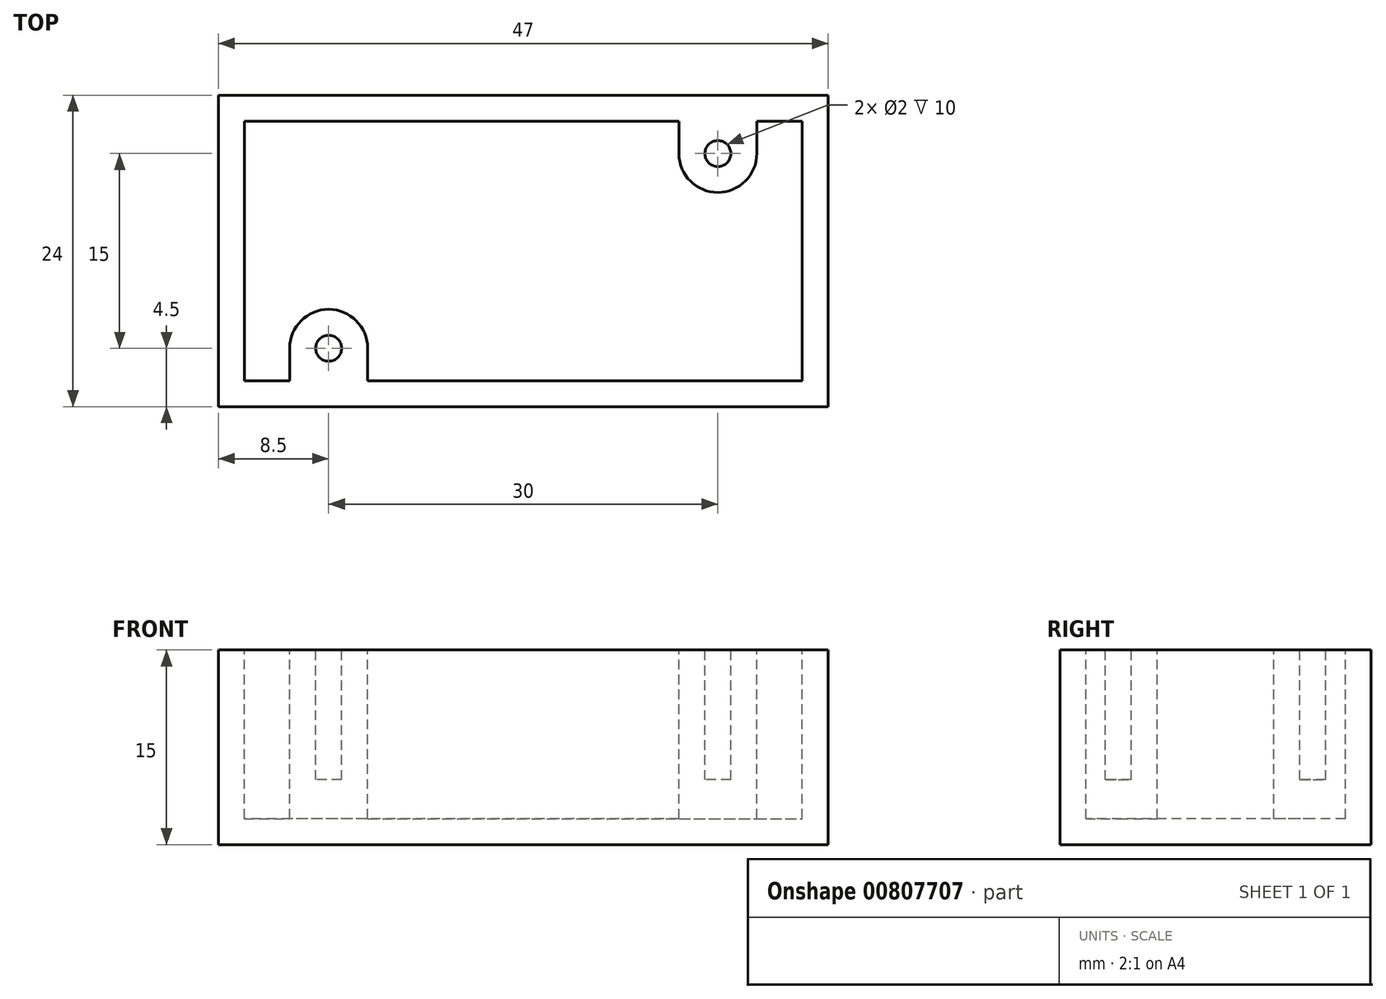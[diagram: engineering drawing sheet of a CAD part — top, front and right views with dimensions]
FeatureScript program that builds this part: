
annotation { "Feature Type Name" : "Feature", "Feature Type Description" : "" }
export const myFeature = defineFeature(function(context is Context, id is Id, definition is map)
    precondition{}
    {
        {
            var Q0;
            Q0=qCreatedBy(makeId("Top.planeOp"),FACE);
            var sketch = newSketch(context, id + "F0", { "sketchPlane" : qUnion([Q0])});
            skLineSegment(sketch, "E0.bottom", {"start": v(-23.5, 12) * mm, "end": v(23.5, 12) * mm});
            skLineSegment(sketch, "E0.top", {"start": v(-23.5, -12) * mm, "end": v(23.5, -12) * mm});
            skLineSegment(sketch, "E0.left", {"start": v(-23.5, 12) * mm, "end": v(-23.5, -12) * mm});
            skLineSegment(sketch, "E0.right", {"start": v(23.5, 12) * mm, "end": v(23.5, -12) * mm});
            skSolve(sketch);
        }
        {
            var Q0;
            Q0 = qSketchRegion(id + "F0", true);
            extrude(context, id + "F1", {"entities" : qUnion([Q0]), "depth" : 15 * mm, "offsetDistance" : 25 * mm});
        }
        {
            var Q0;
            Q0=makeQuery(id+"F1.opExtrude","CAP_FACE",FACE,{"disambiguationData":[OSD([sQuery(id+"F0.wireOp",EDGE,"E0.bottom"),sQuery(id+"F0.wireOp",EDGE,"E0.top"),sQuery(id+"F0.wireOp",EDGE,"E0.left"),sQuery(id+"F0.wireOp",EDGE,"E0.right")])],"isStart":false});
            var sketch = newSketch(context, id + "F2", { "sketchPlane" : qUnion([Q0])});
            skLineSegment(sketch, "E1", {"start": v(18, 10) * mm, "end": v(21.5, 10) * mm});
            skLineSegment(sketch, "E2", {"start": v(21.5, 10) * mm, "end": v(21.5, -10) * mm});
            skLineSegment(sketch, "E3", {"start": v(18, 10) * mm, "end": v(18, 7.5) * mm});
            skArc(sketch, "E4", {"start": v(12, 7.5) * mm, "mid": v(15, 4.5) * mm, "end": v(18, 7.5) * mm});
            skLineSegment(sketch, "E5", {"start": v(12, 7.5) * mm, "end": v(12, 10) * mm});
            skLineSegment(sketch, "E6", {"start": v(12, 10) * mm, "end": v(-21.5, 10) * mm});
            skLineSegment(sketch, "E7", {"start": v(-21.5, 10) * mm, "end": v(-21.5, -10) * mm});
            skLineSegment(sketch, "E8", {"start": v(-21.5, -10) * mm, "end": v(-18, -10) * mm});
            skLineSegment(sketch, "E9", {"start": v(-18, -10) * mm, "end": v(-18, -7.5) * mm});
            skArc(sketch, "E10", {"start": v(-12, -7.5) * mm, "mid": v(-15, -4.5) * mm, "end": v(-18, -7.5) * mm});
            skLineSegment(sketch, "E11", {"start": v(-12, -7.5) * mm, "end": v(-12, -10) * mm});
            skLineSegment(sketch, "E12", {"start": v(-12, -10) * mm, "end": v(21.5, -10) * mm});
            skSolve(sketch);
        }
        {
            var Q0;
            Q0 = qSketchRegion(id + "F2", true);
            extrude(context, id + "F3", {"entities" : qUnion([Q0]), "operationType" : NewBodyOperationType.REMOVE, "oppositeDirection" : true, "depth" : 13 * mm, "offsetDistance" : 25 * mm});
        }
        {
            var Q0;
            Q0=makeQuery(id+"F1.opExtrude","CAP_FACE",FACE,{"disambiguationData":[OSD([sQuery(id+"F0.wireOp",EDGE,"E0.bottom"),sQuery(id+"F0.wireOp",EDGE,"E0.top"),sQuery(id+"F0.wireOp",EDGE,"E0.left"),sQuery(id+"F0.wireOp",EDGE,"E0.right")])],"isStart":false});
            var sketch = newSketch(context, id + "F4", { "sketchPlane" : qUnion([Q0])});
            skCircle(sketch, "E13", {"center": v(15, 7.5) * mm, "radius": 1 * mm});
            skCircle(sketch, "E14", {"center": v(-15, -7.5) * mm, "radius": 1 * mm});
            skSolve(sketch);
        }
        {
            var Q0;
            Q0 = qSketchRegion(id + "F4", true);
            extrude(context, id + "F5", {"entities" : qUnion([Q0]), "operationType" : NewBodyOperationType.REMOVE, "oppositeDirection" : true, "depth" : 10 * mm, "offsetDistance" : 25 * mm});
        }
    });
